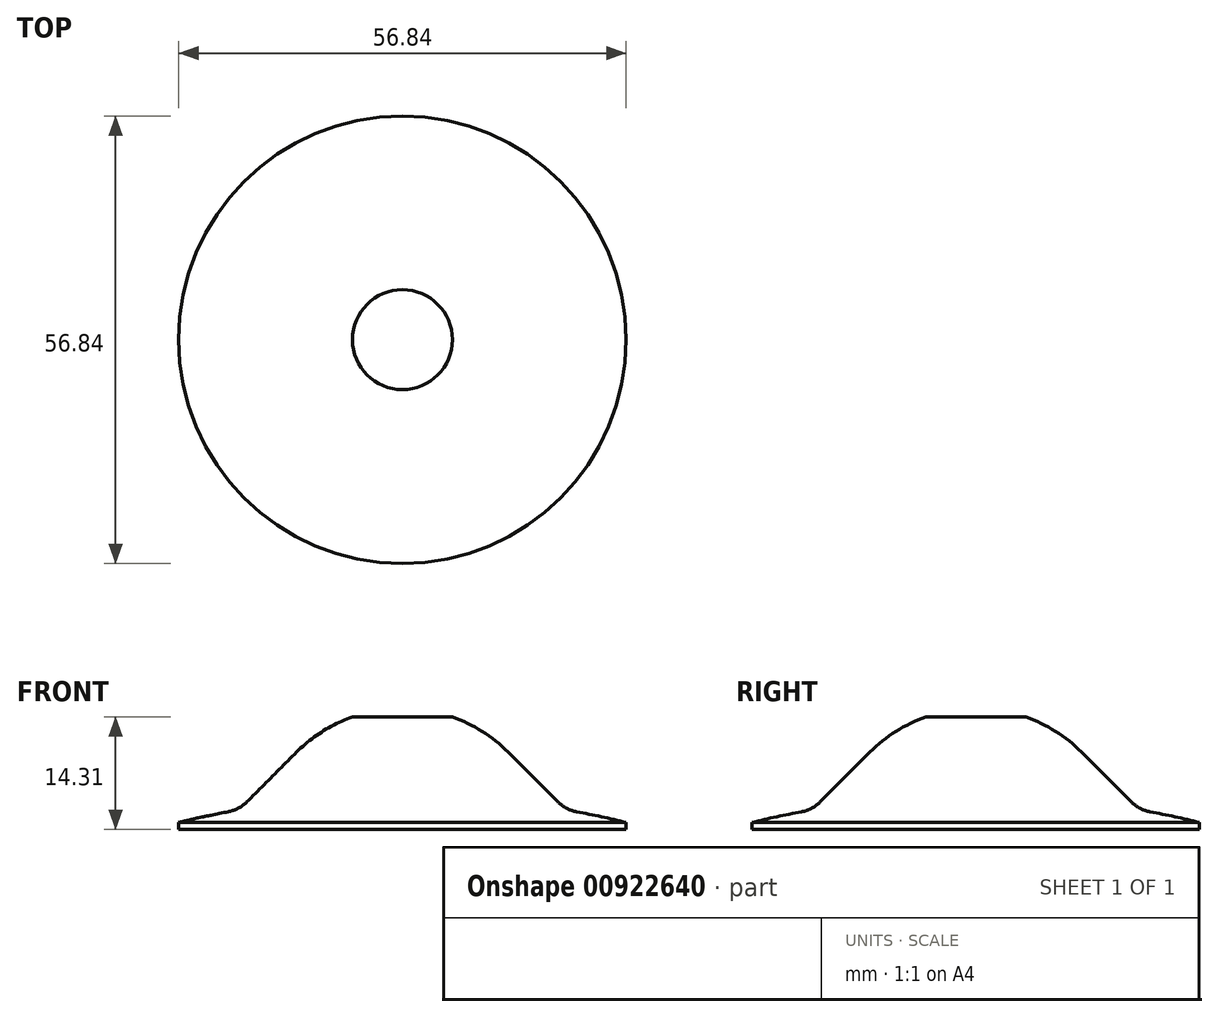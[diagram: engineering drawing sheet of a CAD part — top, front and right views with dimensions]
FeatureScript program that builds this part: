
annotation { "Feature Type Name" : "Feature", "Feature Type Description" : "" }
export const myFeature = defineFeature(function(context is Context, id is Id, definition is map)
    precondition{}
    {
        {
            var Q0;
            Q0=qCreatedBy(makeId("Front.planeOp"),FACE);
            var sketch = newSketch(context, id + "F0", { "sketchPlane" : qUnion([Q0])});
            skLineSegment(sketch, "E0.bottom", {"start": v(28.42, -0.45) * mm, "end": v(-28.42, -0.45) * mm});
            skLineSegment(sketch, "E0.top", {"start": v(28.42, 0.45) * mm, "end": v(-28.42, 0.45) * mm});
            skLineSegment(sketch, "E0.left", {"start": v(28.42, -0.45) * mm, "end": v(28.42, 0.45) * mm});
            skLineSegment(sketch, "E0.right", {"start": v(-28.42, -0.45) * mm, "end": v(-28.42, 0.45) * mm});
            skPoint(sketch, "E0.middle", {"position": v(0, 0) * mm});
            skArc(sketch, "E1", {"start": v(18.46, 0.45) * mm, "mid": v(0, 14.95) * mm, "end": v(-18.46, 0.45) * mm});
            skLineSegment(sketch, "E2", {"start": v(-13.44, 9.39) * mm, "end": v(-20.77, 2.05) * mm});
            skLineSegment(sketch, "E3", {"start": v(13.44, 9.39) * mm, "end": v(20.77, 2.05) * mm});
            skLineSegment(sketch, "E4", {"start": v(0, 0) * mm, "end": v(0, 20.8) * mm});
            skPoint(sketch, "E4.endSnap0", {"position": v(0, 3.33) * mm});
            skLineSegment(sketch, "E5", {"start": v(0, 0) * mm, "end": v(0, -4.05) * mm});
            skLineSegment(sketch, "E6", {"start": v(0, -4.05) * mm, "end": v(0, -166.6) * mm});
            skCircle(sketch, "E7", {"center": v(0, -116.14) * mm, "radius": 120 * mm});
            skCircle(sketch, "E8", {"center": v(-22.95, 6.23) * mm, "radius": 4.5 * mm});
            skLineSegment(sketch, "E9", {"start": v(0, 13.86) * mm, "end": v(-6.35, 13.86) * mm});
            skSolve(sketch);
        }
        {
            var Q0;
            {var subQ0=sQuery(id+"F0.wireOp",EDGE,"E1");var subQ1=makeQuery(id+"F0.imprint","INTERSECT",VERTEX,{"derivedFrom":[subQ0,sQuery(id+"F0.wireOp",EDGE,"E2")]});Q0=makeQuery(id+"F0.imprint","IMPRINT",FACE,{"disambiguationData":[TD([[makeQuery(id+"F0.imprint","IMPRINT",EDGE,{"disambiguationData":[TD([[subQ1,1.0]])],"derivedFrom":subQ0}),1.0]])]});}
            var Q1;
            {var subQ0=sQuery(id+"F0.wireOp",EDGE,"E2");var subQ1=sQuery(id+"F0.wireOp",EDGE,"E1");var subQ2=makeQuery(id+"F0.imprint","INTERSECT",VERTEX,{"derivedFrom":[subQ1,subQ0]});Q1=makeQuery(id+"F0.imprint","IMPRINT",FACE,{"disambiguationData":[TD([[makeQuery(id+"F0.imprint","IMPRINT",EDGE,{"disambiguationData":[TD([[subQ2,-1.0]])],"derivedFrom":subQ1}),-1.0]])]});}
            var Q2;
            {var subQ3=sQuery(id+"F0.wireOp",EDGE,"E1");var subQ4=sQuery(id+"F0.wireOp",EDGE,"E0.top");var subQ5=makeQuery(id+"F0.imprint","INTERSECT",VERTEX,{"disambiguationData":[OD(1.0)],"derivedFrom":[subQ4,subQ3]});Q2=makeQuery(id+"F0.imprint","IMPRINT",FACE,{"disambiguationData":[TD([[makeQuery(id+"F0.imprint","IMPRINT",EDGE,{"disambiguationData":[TD([[subQ5,1.0]])],"derivedFrom":subQ3}),-1.0]])]});}
            var Q3;
            {var subQ0=sQuery(id+"F0.wireOp",EDGE,"E0.right");Q3=makeQuery(id+"F0.imprint","IMPRINT",FACE,{"disambiguationData":[TD([[makeQuery(id+"F0.imprint","IMPRINT",EDGE,{"derivedFrom":subQ0}),-1.0]])]});}
            var Q4;
            {var subQ0=sQuery(id+"F0.wireOp",EDGE,"E7");var subQ1=sQuery(id+"F0.wireOp",EDGE,"E2");var subQ2=makeQuery(id+"F0.imprint","INTERSECT",VERTEX,{"derivedFrom":[subQ1,subQ0]});Q4=makeQuery(id+"F0.imprint","IMPRINT",FACE,{"disambiguationData":[TD([[makeQuery(id+"F0.imprint","IMPRINT",EDGE,{"disambiguationData":[TD([[subQ2,1.0]])],"derivedFrom":subQ1}),-1.0]])]});}
            var Q5;
            {var subQ0=sQuery(id+"F0.wireOp",EDGE,"E1");var subQ1=sQuery(id+"F0.wireOp",EDGE,"E0.top");var subQ2=makeQuery(id+"F0.imprint","INTERSECT",VERTEX,{"disambiguationData":[OD(1.0)],"derivedFrom":[subQ1,subQ0]});Q5=makeQuery(id+"F0.imprint","IMPRINT",FACE,{"disambiguationData":[TD([[makeQuery(id+"F0.imprint","IMPRINT",EDGE,{"disambiguationData":[TD([[subQ2,1.0]])],"derivedFrom":subQ1}),-1.0]])]});}
            var Q6;
            Q6=sQuery(id+"F0.wireOp",EDGE,"E4");
            revolve(context, id + "F1", {"surfaceOperationType" : NewSurfaceOperationType.NEW, "entities" : qUnion([Q0, Q1, Q2, Q3, Q4, Q5]), "axis" : qUnion([Q6]), "revolveType" : RevolveType.FULL});
        }
    });
